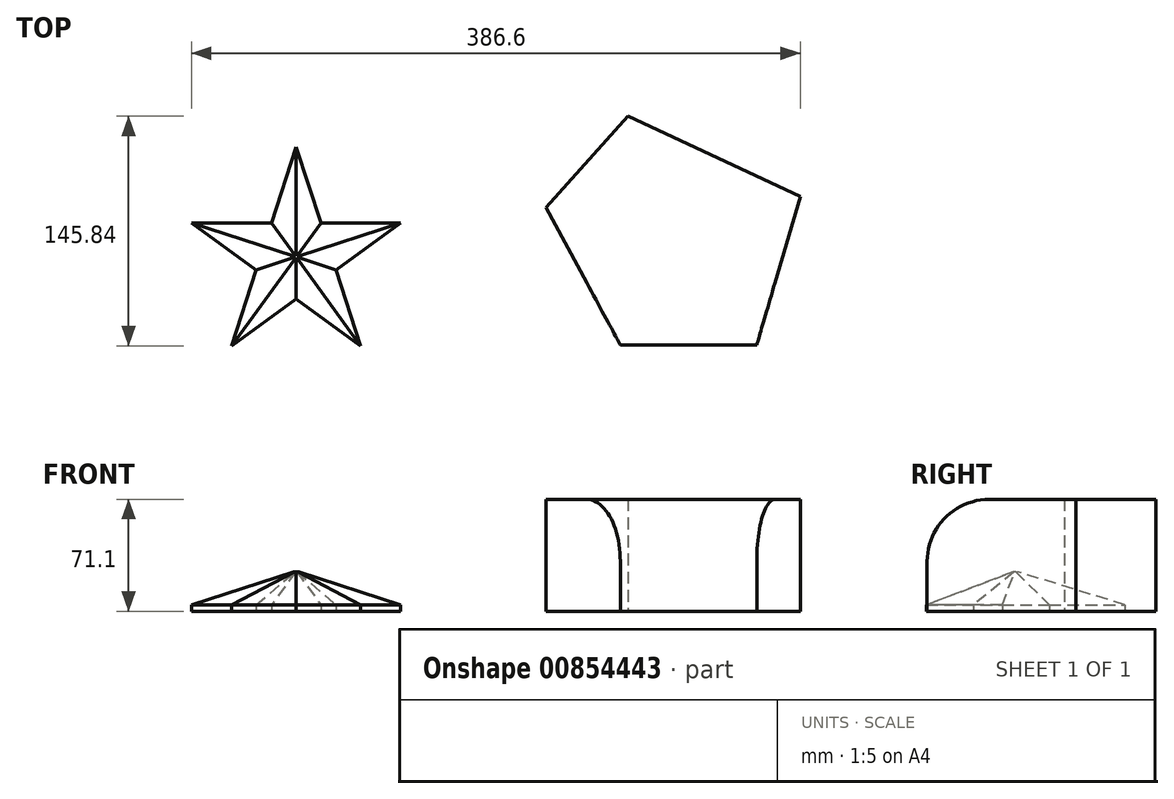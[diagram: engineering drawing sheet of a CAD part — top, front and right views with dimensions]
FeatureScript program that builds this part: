
annotation { "Feature Type Name" : "Feature", "Feature Type Description" : "" }
export const myFeature = defineFeature(function(context is Context, id is Id, definition is map)
    precondition{}
    {
        {
            var Q0;
            Q0=qCreatedBy(makeId("Top.planeOp"),FACE);
            var sketch = newSketch(context, id + "F0", { "sketchPlane" : qUnion([Q0])});
            skCircle(sketch, "E0.cCircle", {"center": v(0, 0) * mm, "radius": 56.5 * mm, "construction": true});
            skLineSegment(sketch, "E0.0", {"start": v(41.05, -56.5) * mm, "end": v(-41.05, -56.5) * mm});
            skLineSegment(sketch, "E0.1", {"start": v(-41.05, -56.5) * mm, "end": v(-66.42, 21.58) * mm});
            skLineSegment(sketch, "E0.2", {"start": v(-66.42, 21.58) * mm, "end": v(0, 69.84) * mm});
            skLineSegment(sketch, "E0.3", {"start": v(0, 69.84) * mm, "end": v(66.42, 21.58) * mm});
            skLineSegment(sketch, "E0.4", {"start": v(66.42, 21.58) * mm, "end": v(41.05, -56.5) * mm});
            skPoint(sketch, "E0.0.midPoint", {"position": v(0, -56.5) * mm});
            skLineSegment(sketch, "E1", {"start": v(0, 69.84) * mm, "end": v(-41.05, -56.5) * mm});
            skLineSegment(sketch, "E2", {"start": v(0, 69.84) * mm, "end": v(41.05, -56.5) * mm});
            skLineSegment(sketch, "E3", {"start": v(-66.42, 21.58) * mm, "end": v(66.42, 21.58) * mm});
            skLineSegment(sketch, "E4", {"start": v(-66.42, 21.58) * mm, "end": v(41.05, -56.5) * mm});
            skLineSegment(sketch, "E5", {"start": v(66.42, 21.58) * mm, "end": v(-41.05, -56.5) * mm});
            skSolve(sketch);
        }
        {
            var Q0;
            {var subQ1=sQuery(id+"F0.wireOp",EDGE,"E1");var subQ3=sQuery(id+"F0.wireOp",EDGE,"E3");var subQ4=makeQuery(id+"F0.imprint","INTERSECT",VERTEX,{"derivedFrom":[subQ1,subQ3]});Q0=makeQuery(id+"F0.imprint","IMPRINT",FACE,{"disambiguationData":[TD([[makeQuery(id+"F0.imprint","IMPRINT",EDGE,{"disambiguationData":[TD([[subQ4,-1.0]])],"derivedFrom":subQ3}),1.0]])]});}
            var Q1;
            {var subQ1=sQuery(id+"F0.wireOp",EDGE,"E1");var subQ5=sQuery(id+"F0.wireOp",EDGE,"E3");var subQ6=makeQuery(id+"F0.imprint","INTERSECT",VERTEX,{"derivedFrom":[subQ1,subQ5]});Q1=makeQuery(id+"F0.imprint","IMPRINT",FACE,{"disambiguationData":[TD([[makeQuery(id+"F0.imprint","IMPRINT",EDGE,{"disambiguationData":[TD([[subQ6,-1.0]])],"derivedFrom":subQ1}),1.0]])]});}
            var Q2;
            {var subQ0=sQuery(id+"F0.wireOp",EDGE,"E3");var subQ1=sQuery(id+"F0.wireOp",EDGE,"E1");var subQ2=makeQuery(id+"F0.imprint","INTERSECT",VERTEX,{"derivedFrom":[subQ1,subQ0]});Q2=makeQuery(id+"F0.imprint","IMPRINT",FACE,{"disambiguationData":[TD([[makeQuery(id+"F0.imprint","IMPRINT",EDGE,{"disambiguationData":[TD([[subQ2,-1.0]])],"derivedFrom":subQ1}),-1.0]])]});}
            var Q3;
            {var subQ1=sQuery(id+"F0.wireOp",EDGE,"E1");var subQ3=sQuery(id+"F0.wireOp",EDGE,"E4");var subQ4=makeQuery(id+"F0.imprint","INTERSECT",VERTEX,{"derivedFrom":[subQ1,subQ3]});Q3=makeQuery(id+"F0.imprint","IMPRINT",FACE,{"disambiguationData":[TD([[makeQuery(id+"F0.imprint","IMPRINT",EDGE,{"disambiguationData":[TD([[subQ4,-1.0]])],"derivedFrom":subQ3}),-1.0]])]});}
            var Q4;
            {var subQ1=sQuery(id+"F0.wireOp",EDGE,"E2");var subQ3=sQuery(id+"F0.wireOp",EDGE,"E5");var subQ4=makeQuery(id+"F0.imprint","INTERSECT",VERTEX,{"derivedFrom":[subQ1,subQ3]});Q4=makeQuery(id+"F0.imprint","IMPRINT",FACE,{"disambiguationData":[TD([[makeQuery(id+"F0.imprint","IMPRINT",EDGE,{"disambiguationData":[TD([[subQ4,-1.0]])],"derivedFrom":subQ3}),1.0]])]});}
            var Q5;
            {var subQ0=sQuery(id+"F0.wireOp",EDGE,"E3");var subQ1=sQuery(id+"F0.wireOp",EDGE,"E2");var subQ2=makeQuery(id+"F0.imprint","INTERSECT",VERTEX,{"derivedFrom":[subQ1,subQ0]});Q5=makeQuery(id+"F0.imprint","IMPRINT",FACE,{"disambiguationData":[TD([[makeQuery(id+"F0.imprint","IMPRINT",EDGE,{"disambiguationData":[TD([[subQ2,-1.0]])],"derivedFrom":subQ1}),1.0]])]});}
            extrude(context, id + "F1", {"entities" : qUnion([Q0, Q1, Q2, Q3, Q4, Q5]), "depth" : 25 * mm, "offsetDistance" : 25 * mm});
        }
        {
            var Q0;
            Q0=makeQuery(id+"F1.opExtrude","CAP_FACE",FACE,{"disambiguationData":[OSD([sQuery(id+"F0.wireOp",EDGE,"E1"),sQuery(id+"F0.wireOp",EDGE,"E2"),sQuery(id+"F0.wireOp",EDGE,"E3"),sQuery(id+"F0.wireOp",EDGE,"E4"),sQuery(id+"F0.wireOp",EDGE,"E5")])],"isStart":false});
            chamfer(context, id + "F2", {"entities" : qUnion([Q0]), "width" : 21 * mm, "tangentPropagation" : true});
        }
        {
            var Q0;
            Q0=qCreatedBy(makeId("Top.planeOp"),FACE);
            var sketch = newSketch(context, id + "F3", { "sketchPlane" : qUnion([Q0])});
            skLineSegment(sketch, "E6", {"start": v(158.62, 31.33) * mm, "end": v(210.8, 89.34) * mm});
            skLineSegment(sketch, "E7", {"start": v(210.8, 89.34) * mm, "end": v(320.18, 38.43) * mm});
            skLineSegment(sketch, "E8", {"start": v(320.18, 38.43) * mm, "end": v(292.57, -55.92) * mm});
            skLineSegment(sketch, "E9", {"start": v(292.57, -55.92) * mm, "end": v(205.9, -55.92) * mm});
            skLineSegment(sketch, "E10", {"start": v(205.9, -55.92) * mm, "end": v(158.62, 31.33) * mm});
            skSolve(sketch);
        }
        {
            var Q0;
            Q0=makeQuery(id+"F3.imprint","IMPRINT",FACE,{"disambiguationData":[TD([[makeQuery(id+"F3.imprint","IMPRINT",EDGE,{"derivedFrom":sQuery(id+"F3.wireOp",EDGE,"E6")}),-1.0]])]});
            extrude(context, id + "F4", {"entities" : qUnion([Q0]), "depth" : 71.1 * mm, "offsetDistance" : 25 * mm});
        }
        {
            var Q0;
            Q0=makeQuery(id+"F4.opExtrude","CAP_EDGE",EDGE,{"disambiguationData":[OSD([sQuery(id+"F3.wireOp",EDGE,"E9")])],"isStart":false});
            fillet(context, id + "F5", {"entities" : qUnion([Q0]), "radius" : 39.35 * mm, "tangentPropagation" : true, "allowEdgeOverflow" : false});
        }
    });
